# Revit family: Haworth_BesideStorage_Pantry_Limited
name_source: partatom
category: Furniture Systems
revit_build: Autodesk Revit 2018 (Build: 20170223_1515(x64)
units: mm (PartAtom-declared; Revit-internal decimal feet)

## family parameters
Always vertical = Yes
Cut with Voids When Loaded = No
OmniClass Number = 23.40.70.14.64.21
OmniClass Title = Systems Furniture
Part Type = Normal
Room Calculation Point = No
Round Connector Dimension = Use Diameter
Shared = No
Work Plane-Based = No

## types (1)
- 31.5d 15w 48h
    Actual Depth = 24"
    Actual Height = 28"
    Actual Width = 15"
    Assembly Code = E2020200
    Base Height = 3/8"
    Custom Depth = Yes
    Custom Height = Yes
    Custom Size = Yes
    Custom Width = Yes
    Depth = 24"
    Door Height = 26 3/4"
    Door Width = 14 7/8"
    Height = 28"
    Manufacturer = Haworth
    Max. Depth = 31 1/2"
    Max. Height = 64 1/2"
    Max. Width = 18"
    Min. Depth = 18 3/4"
    Min. Height = 28"
    Min. Width = 12"
    Panel Thickness = 3/4"
    Pull Height = 13 3/8"
    Revision Number = 1
    Size = Verify Final Dim. w/ Haworth
    Standard Depths = 24, 30 in.
    Standard Heights = 28, 40, 48 in.
    Standard Widths = 12, 15, 18 in.
    Top Height = 3/4"
    URL = http://www.haworth.com
    URL - Product = https://www.haworth.com
    Warranty = http://www.haworth.com
    Width = 15"

## geometry (parser evidence)
native form markers: Blend x4, Sweep x4
no freeform markers — native parametric forms only
